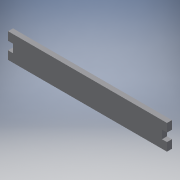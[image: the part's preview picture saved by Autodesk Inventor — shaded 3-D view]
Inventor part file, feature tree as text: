
AUTODESK INVENTOR PART (.ipt)
format: ipt  version: 2019 (Build 230136000, 136)  size: 109,568 bytes
history: native  units: mm
features: other x1, extrude x1, sketch x1
ambient origin geometry x8: Origin, YZ Plane, XZ Plane, XY Plane, X Axis, Y Axis, Z Axis, Center Point
bodies: Body1 (feature_tree)
feature tree (3):
  other  "Твердое тело1"
  extrude  "Выдавливание1"  Depth=180.0mm
  sketch  "Эскиз1"
